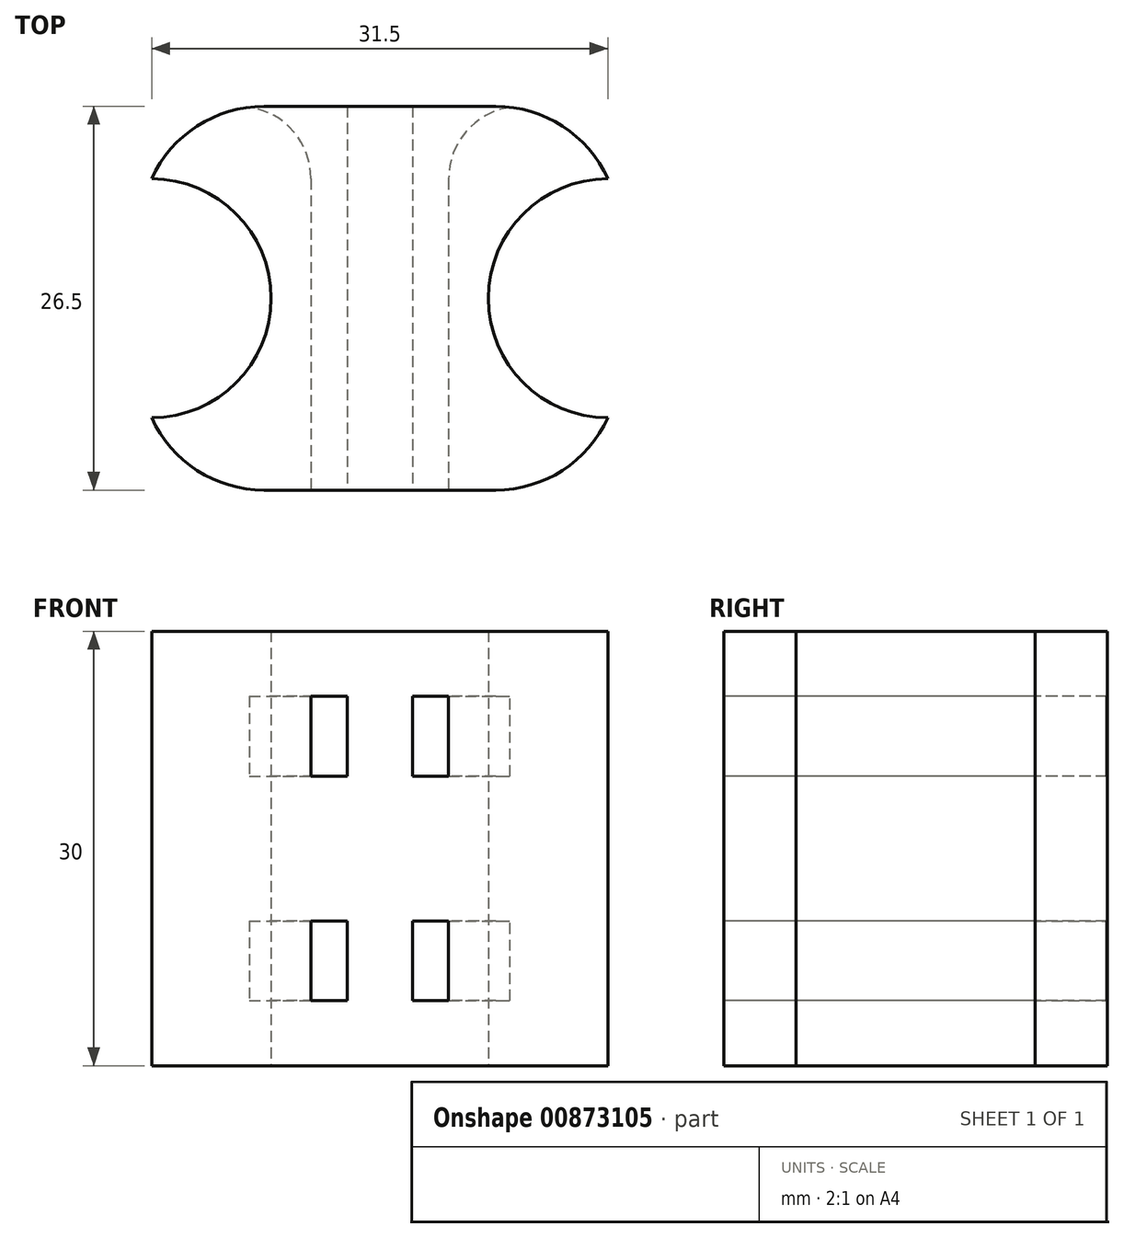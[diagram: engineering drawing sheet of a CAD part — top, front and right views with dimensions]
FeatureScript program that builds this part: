
annotation { "Feature Type Name" : "Feature", "Feature Type Description" : "" }
export const myFeature = defineFeature(function(context is Context, id is Id, definition is map)
    precondition{}
    {
        {
            var Q0;
            Q0=qCreatedBy(makeId("Top.planeOp"),FACE);
            var sketch = newSketch(context, id + "F0", { "sketchPlane" : qUnion([Q0])});
            skLineSegment(sketch, "E0.bottom", {"start": v(-15.75, 13.25) * mm, "end": v(15.75, 13.25) * mm});
            skLineSegment(sketch, "E0.top", {"start": v(-15.75, -13.25) * mm, "end": v(15.75, -13.25) * mm});
            skLineSegment(sketch, "E0.left", {"start": v(-15.75, 13.25) * mm, "end": v(-15.75, -13.25) * mm});
            skLineSegment(sketch, "E0.right", {"start": v(15.75, 13.25) * mm, "end": v(15.75, -13.25) * mm});
            skPoint(sketch, "E0.middle", {"position": v(0, 0) * mm});
            skCircle(sketch, "E1", {"center": v(-15.75, 0) * mm, "radius": 8.25 * mm});
            skCircle(sketch, "E2", {"center": v(15.75, 0) * mm, "radius": 8.25 * mm});
            skSolve(sketch);
        }
        {
            var Q0;
            {var subQ4=sQuery(id+"F0.wireOp",EDGE,"E0.bottom");Q0=makeQuery(id+"F0.imprint","IMPRINT",FACE,{"disambiguationData":[TD([[makeQuery(id+"F0.imprint","IMPRINT",EDGE,{"derivedFrom":subQ4}),-1.0]])]});}
            extrude(context, id + "F1", {"entities" : qUnion([Q0]), "depth" : 30 * mm, "offsetDistance" : 25 * mm});
        }
        {
            var Q0;
            Q0=makeQuery(id+"F1.opExtrude","SWEPT_FACE",FACE,{"disambiguationData":[OSD([sQuery(id+"F0.wireOp",EDGE,"E0.top")])]});
            var sketch = newSketch(context, id + "F2", { "sketchPlane" : qUnion([Q0])});
            skLineSegment(sketch, "E3.bottom", {"start": v(-4.75, 10) * mm, "end": v(-2.25, 10) * mm});
            skLineSegment(sketch, "E3.top", {"start": v(-4.75, 4.5) * mm, "end": v(-2.25, 4.5) * mm});
            skLineSegment(sketch, "E3.left", {"start": v(-4.75, 10) * mm, "end": v(-4.75, 4.5) * mm});
            skLineSegment(sketch, "E3.right", {"start": v(-2.25, 10) * mm, "end": v(-2.25, 4.5) * mm});
            skLineSegment(sketch, "E4.bottom", {"start": v(-4.75, 25.5) * mm, "end": v(-2.25, 25.5) * mm});
            skLineSegment(sketch, "E4.top", {"start": v(-4.75, 20) * mm, "end": v(-2.25, 20) * mm});
            skLineSegment(sketch, "E4.left", {"start": v(-4.75, 25.5) * mm, "end": v(-4.75, 20) * mm});
            skLineSegment(sketch, "E4.right", {"start": v(-2.25, 25.5) * mm, "end": v(-2.25, 20) * mm});
            skLineSegment(sketch, "E5.bottom", {"start": v(2.25, 25.5) * mm, "end": v(4.75, 25.5) * mm});
            skLineSegment(sketch, "E5.top", {"start": v(2.25, 20) * mm, "end": v(4.75, 20) * mm});
            skLineSegment(sketch, "E5.left", {"start": v(2.25, 25.5) * mm, "end": v(2.25, 20) * mm});
            skLineSegment(sketch, "E5.right", {"start": v(4.75, 25.5) * mm, "end": v(4.75, 20) * mm});
            skLineSegment(sketch, "E6.bottom", {"start": v(2.25, 10) * mm, "end": v(4.75, 10) * mm});
            skLineSegment(sketch, "E6.top", {"start": v(2.25, 4.5) * mm, "end": v(4.75, 4.5) * mm});
            skLineSegment(sketch, "E6.left", {"start": v(2.25, 10) * mm, "end": v(2.25, 4.5) * mm});
            skLineSegment(sketch, "E6.right", {"start": v(4.75, 10) * mm, "end": v(4.75, 4.5) * mm});
            skSolve(sketch);
        }
        {
            var Q0;
            Q0=makeQuery(id+"F2.imprint","IMPRINT",FACE,{"disambiguationData":[TD([[makeQuery(id+"F2.imprint","IMPRINT",EDGE,{"derivedFrom":sQuery(id+"F2.wireOp",EDGE,"E4.bottom")}),-1.0]])]});
            var Q1;
            Q1=makeQuery(id+"F2.imprint","IMPRINT",FACE,{"disambiguationData":[TD([[makeQuery(id+"F2.imprint","IMPRINT",EDGE,{"derivedFrom":sQuery(id+"F2.wireOp",EDGE,"E3.bottom")}),-1.0]])]});
            var Q2;
            Q2=makeQuery(id+"F2.imprint","IMPRINT",FACE,{"disambiguationData":[TD([[makeQuery(id+"F2.imprint","IMPRINT",EDGE,{"derivedFrom":sQuery(id+"F2.wireOp",EDGE,"E5.bottom")}),-1.0]])]});
            var Q3;
            Q3=makeQuery(id+"F2.imprint","IMPRINT",FACE,{"disambiguationData":[TD([[makeQuery(id+"F2.imprint","IMPRINT",EDGE,{"derivedFrom":sQuery(id+"F2.wireOp",EDGE,"E6.bottom")}),-1.0]])]});
            extrude(context, id + "F3", {"entities" : qUnion([Q0, Q1, Q2, Q3]), "operationType" : NewBodyOperationType.REMOVE, "oppositeDirection" : true, "depth" : 27 * mm, "offsetDistance" : 25 * mm});
        }
        {
            var Q0;
            Q0=makeQuery(id+"F1.opExtrude","SWEPT_EDGE",EDGE,{"disambiguationData":[OSD([sQuery(id+"F0.wireOp",EDGE,"E0.bottom"),sQuery(id+"F0.wireOp",EDGE,"E0.left")])]});
            var Q1;
            Q1=makeQuery(id+"F1.opExtrude","SWEPT_EDGE",EDGE,{"disambiguationData":[OSD([sQuery(id+"F0.wireOp",EDGE,"E0.top"),sQuery(id+"F0.wireOp",EDGE,"E0.left")])]});
            var Q2;
            Q2=makeQuery(id+"F1.opExtrude","SWEPT_EDGE",EDGE,{"disambiguationData":[OSD([sQuery(id+"F0.wireOp",EDGE,"E0.top"),sQuery(id+"F0.wireOp",EDGE,"E0.right")])]});
            var Q3;
            Q3=makeQuery(id+"F1.opExtrude","SWEPT_EDGE",EDGE,{"disambiguationData":[OSD([sQuery(id+"F0.wireOp",EDGE,"E0.bottom"),sQuery(id+"F0.wireOp",EDGE,"E0.right")])]});
            fillet(context, id + "F4", {"entities" : qUnion([Q0, Q1, Q2, Q3]), "radius" : 8.5 * mm, "tangentPropagation" : true, "allowEdgeOverflow" : false});
        }
        {
            var Q0;
            Q0=makeQuery(id+"F3.boolean.opBoolean","COPY",EDGE,{"derivedFrom":makeQuery(id+"F3.opExtrude","CAP_EDGE",EDGE,{"disambiguationData":[OSD([sQuery(id+"F2.wireOp",EDGE,"E4.left")])],"isStart":true})});
            var Q1;
            Q1=makeQuery(id+"F3.boolean.opBoolean","COPY",EDGE,{"derivedFrom":makeQuery(id+"F3.opExtrude","CAP_EDGE",EDGE,{"disambiguationData":[OSD([sQuery(id+"F2.wireOp",EDGE,"E3.left")])],"isStart":true})});
            var Q2;
            Q2=makeQuery(id+"F3.boolean.opBoolean","COPY",EDGE,{"derivedFrom":makeQuery(id+"F3.opExtrude","CAP_EDGE",EDGE,{"disambiguationData":[OSD([sQuery(id+"F2.wireOp",EDGE,"E5.right")])],"isStart":true})});
            var Q3;
            Q3=makeQuery(id+"F3.boolean.opBoolean","COPY",EDGE,{"derivedFrom":makeQuery(id+"F3.opExtrude","CAP_EDGE",EDGE,{"disambiguationData":[OSD([sQuery(id+"F2.wireOp",EDGE,"E6.right")])],"isStart":true})});
            var Q4;
            Q4=makeQuery(id+"F3.boolean.opBoolean","INTERSECT",EDGE,{"derivedFrom":[makeQuery(id+"F1.opExtrude","SWEPT_FACE",FACE,{"disambiguationData":[OSD([sQuery(id+"F0.wireOp",EDGE,"E0.bottom")])]}),makeQuery(id+"F3.opExtrude","SWEPT_FACE",FACE,{"disambiguationData":[OSD([sQuery(id+"F2.wireOp",EDGE,"E5.right")])]})]});
            var Q5;
            Q5=makeQuery(id+"F3.boolean.opBoolean","INTERSECT",EDGE,{"derivedFrom":[makeQuery(id+"F1.opExtrude","SWEPT_FACE",FACE,{"disambiguationData":[OSD([sQuery(id+"F0.wireOp",EDGE,"E0.bottom")])]}),makeQuery(id+"F3.opExtrude","SWEPT_FACE",FACE,{"disambiguationData":[OSD([sQuery(id+"F2.wireOp",EDGE,"E6.right")])]})]});
            var Q6;
            Q6=makeQuery(id+"F3.boolean.opBoolean","INTERSECT",EDGE,{"derivedFrom":[makeQuery(id+"F1.opExtrude","SWEPT_FACE",FACE,{"disambiguationData":[OSD([sQuery(id+"F0.wireOp",EDGE,"E0.bottom")])]}),makeQuery(id+"F3.opExtrude","SWEPT_FACE",FACE,{"disambiguationData":[OSD([sQuery(id+"F2.wireOp",EDGE,"E4.left")])]})]});
            var Q7;
            Q7=makeQuery(id+"F3.boolean.opBoolean","INTERSECT",EDGE,{"derivedFrom":[makeQuery(id+"F1.opExtrude","SWEPT_FACE",FACE,{"disambiguationData":[OSD([sQuery(id+"F0.wireOp",EDGE,"E0.bottom")])]}),makeQuery(id+"F3.opExtrude","SWEPT_FACE",FACE,{"disambiguationData":[OSD([sQuery(id+"F2.wireOp",EDGE,"E3.left")])]})]});
            fillet(context, id + "F5", {"entities" : qUnion([Q0, Q1, Q2, Q3, Q4, Q5, Q6, Q7]), "radius" : 5 * mm, "tangentPropagation" : true, "allowEdgeOverflow" : false});
        }
    });
